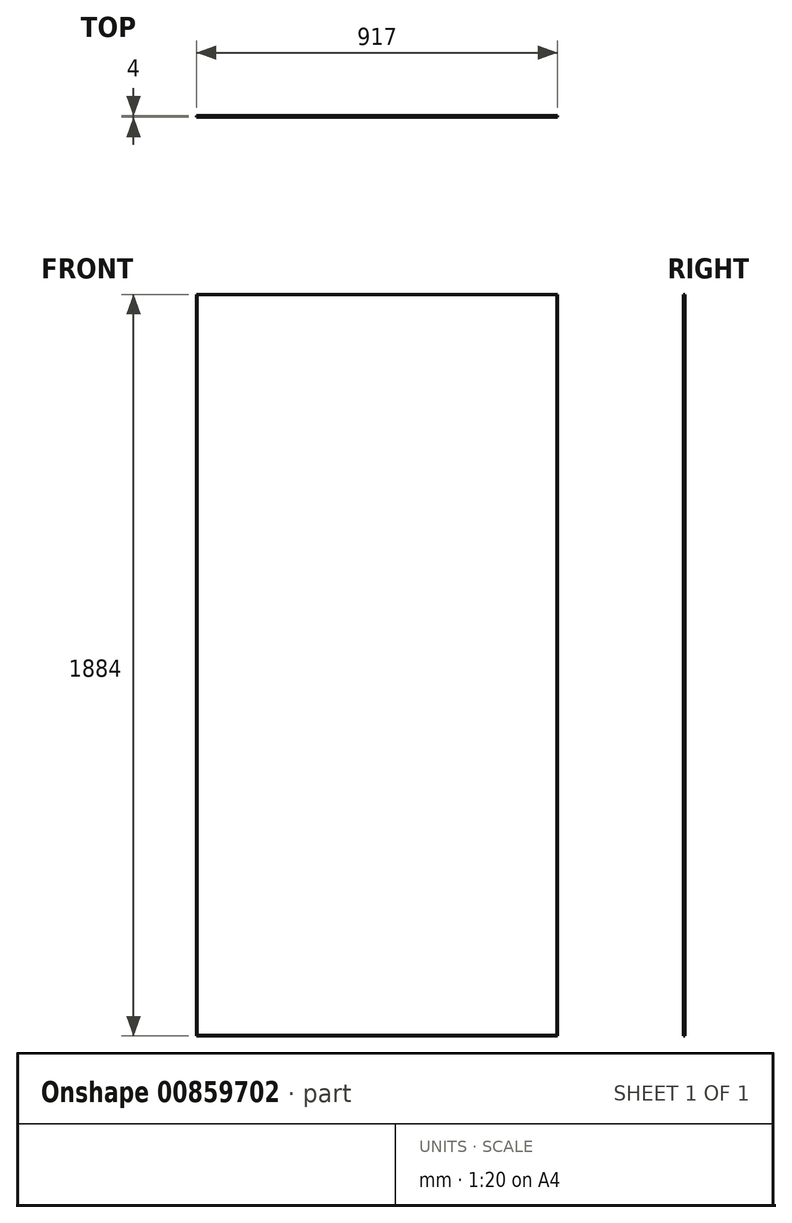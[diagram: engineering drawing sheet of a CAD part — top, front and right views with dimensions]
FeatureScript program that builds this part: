
annotation { "Feature Type Name" : "Feature", "Feature Type Description" : "" }
export const myFeature = defineFeature(function(context is Context, id is Id, definition is map)
    precondition{}
    {
        {
            var Q0;
            Q0=qCreatedBy(makeId("Top.planeOp"),FACE);
            var sketch = newSketch(context, id + "F0", { "sketchPlane" : qUnion([Q0])});
            skLineSegment(sketch, "E0.bottom", {"start": v(-942, 458.5) * mm, "end": v(942, 458.5) * mm});
            skLineSegment(sketch, "E0.top", {"start": v(-942, -458.5) * mm, "end": v(942, -458.5) * mm});
            skLineSegment(sketch, "E0.left", {"start": v(-942, 458.5) * mm, "end": v(-942, -458.5) * mm});
            skLineSegment(sketch, "E0.right", {"start": v(942, 458.5) * mm, "end": v(942, -458.5) * mm});
            skPoint(sketch, "E0.middle", {"position": v(0, 0) * mm});
            skSolve(sketch);
        }
        {
            var Q0;
            Q0=makeQuery(id+"F0.imprint","IMPRINT",FACE,{"disambiguationData":[TD([[makeQuery(id+"F0.imprint","IMPRINT",EDGE,{"derivedFrom":sQuery(id+"F0.wireOp",EDGE,"E0.bottom")}),-1.0]])]});
            extrude(context, id + "F1", {"entities" : qUnion([Q0]), "endBound" : BoundingType.SYMMETRIC, "depth" : 4 * mm, "offsetDistance" : 25 * mm});
        }
        {
            var Q0;
            Q0=makeQuery(id+"F1.opExtrude","CAP_EDGE",EDGE,{"disambiguationData":[OSD([sQuery(id+"F0.wireOp",EDGE,"E0.right")])],"isStart":true});
            var Q1;
            Q1=makeQuery(id+"F1.opExtrude","CAP_EDGE",EDGE,{"disambiguationData":[OSD([sQuery(id+"F0.wireOp",EDGE,"E0.top")])],"isStart":true});
            var Q2;
            Q2=makeQuery(id+"F1.opExtrude","CAP_EDGE",EDGE,{"disambiguationData":[OSD([sQuery(id+"F0.wireOp",EDGE,"E0.left")])],"isStart":true});
            var Q3;
            Q3=makeQuery(id+"F1.opExtrude","CAP_EDGE",EDGE,{"disambiguationData":[OSD([sQuery(id+"F0.wireOp",EDGE,"E0.bottom")])],"isStart":true});
            chamfer(context, id + "F2", {"entities" : qUnion([Q0, Q1, Q2, Q3]), "width" : 1 * mm, "tangentPropagation" : true});
        }
        {
            var Q0;
            Q0=makeQuery(id+"F1.opExtrude","SWEPT_EDGE",EDGE,{"disambiguationData":[OSD([sQuery(id+"F0.wireOp",EDGE,"E0.top"),sQuery(id+"F0.wireOp",EDGE,"E0.right")])]});
            chamfer(context, id + "F3", {"entities" : qUnion([Q0]), "width" : 1 * mm, "tangentPropagation" : true});
        }
        {
            var Q0;
            Q0=makeQuery(id+"F1.opExtrude","SWEPT_EDGE",EDGE,{"disambiguationData":[OSD([sQuery(id+"F0.wireOp",EDGE,"E0.bottom"),sQuery(id+"F0.wireOp",EDGE,"E0.left")])]});
            chamfer(context, id + "F4", {"entities" : qUnion([Q0]), "width" : 1 * mm, "tangentPropagation" : true});
        }
        {
            var Q0;
            Q0=makeQuery(id+"F1.opExtrude","SWEPT_EDGE",EDGE,{"disambiguationData":[OSD([sQuery(id+"F0.wireOp",EDGE,"E0.top"),sQuery(id+"F0.wireOp",EDGE,"E0.left")])]});
            chamfer(context, id + "F5", {"entities" : qUnion([Q0]), "width" : 1 * mm, "tangentPropagation" : true});
        }
        {
            var Q0;
            Q0=makeQuery(id+"F1.opExtrude","SWEPT_EDGE",EDGE,{"disambiguationData":[OSD([sQuery(id+"F0.wireOp",EDGE,"E0.bottom"),sQuery(id+"F0.wireOp",EDGE,"E0.right")])]});
            chamfer(context, id + "F6", {"entities" : qUnion([Q0]), "width" : 1 * mm, "tangentPropagation" : true});
        }
        {
            var Q0;
            Q0=makeQuery(id+"F1.opExtrude","CAP_EDGE",EDGE,{"disambiguationData":[OSD([sQuery(id+"F0.wireOp",EDGE,"E0.top")])],"isStart":false});
            var Q1;
            Q1=makeQuery(id+"F1.opExtrude","CAP_EDGE",EDGE,{"disambiguationData":[OSD([sQuery(id+"F0.wireOp",EDGE,"E0.right")])],"isStart":false});
            var Q2;
            Q2=makeQuery(id+"F1.opExtrude","CAP_EDGE",EDGE,{"disambiguationData":[OSD([sQuery(id+"F0.wireOp",EDGE,"E0.bottom")])],"isStart":false});
            var Q3;
            Q3=makeQuery(id+"F1.opExtrude","CAP_EDGE",EDGE,{"disambiguationData":[OSD([sQuery(id+"F0.wireOp",EDGE,"E0.left")])],"isStart":false});
            chamfer(context, id + "F7", {"entities" : qUnion([Q0, Q1, Q2, Q3]), "width" : 1 * mm, "tangentPropagation" : true});
        }
        {
            var Q0;
            Q0=makeQuery(id+"F1.opExtrude","SWEPT_BODY",BODY,{"disambiguationData":[OSD([sQuery(id+"F0.wireOp",EDGE,"E0.bottom"),sQuery(id+"F0.wireOp",EDGE,"E0.top"),sQuery(id+"F0.wireOp",EDGE,"E0.left"),sQuery(id+"F0.wireOp",EDGE,"E0.right")])]});
            var Q1;
            {var subQ0=sQuery(id+"F0.wireOp",EDGE,"E0.right");Q1=makeQuery(id+"F2.opChamfer","BLEND_EDGE",EDGE,{"blendedFrom":[makeQuery(id+"F1.opExtrude","CAP_EDGE",EDGE,{"disambiguationData":[OSD([subQ0])],"isStart":true}),makeQuery(id+"F1.opExtrude","SWEPT_FACE",FACE,{"disambiguationData":[OSD([subQ0])]})],"blendedInto":[makeQuery(id+"F1.opExtrude","SWEPT_FACE",FACE,{"disambiguationData":[OSD([subQ0])]})]});}
            transform(context, id + "F8", {"entities" : qUnion([Q0]), "transformType" : TransformType.ROTATION, "transformAxis" : qUnion([Q1]), "angle" : 90 * degree, "makeCopy" : false});
        }
        {
            var Q0;
            Q0=makeQuery(id+"F1.opExtrude","SWEPT_BODY",BODY,{"disambiguationData":[OSD([sQuery(id+"F0.wireOp",EDGE,"E0.bottom"),sQuery(id+"F0.wireOp",EDGE,"E0.top"),sQuery(id+"F0.wireOp",EDGE,"E0.left"),sQuery(id+"F0.wireOp",EDGE,"E0.right")])]});
            var Q1;
            {var subQ0=sQuery(id+"F0.wireOp",EDGE,"E0.bottom");Q1=makeQuery(id+"F7.opChamfer","BLEND_EDGE",EDGE,{"blendedFrom":[makeQuery(id+"F1.opExtrude","CAP_EDGE",EDGE,{"disambiguationData":[OSD([subQ0])],"isStart":false}),makeQuery(id+"F1.opExtrude","SWEPT_FACE",FACE,{"disambiguationData":[OSD([subQ0])]})],"blendedInto":[makeQuery(id+"F1.opExtrude","SWEPT_FACE",FACE,{"disambiguationData":[OSD([subQ0])]})]});}
            transform(context, id + "F9", {"entities" : qUnion([Q0]), "transformType" : TransformType.ROTATION, "transformAxis" : qUnion([Q1]), "angle" : 90 * degree, "makeCopy" : false});
        }
    });
